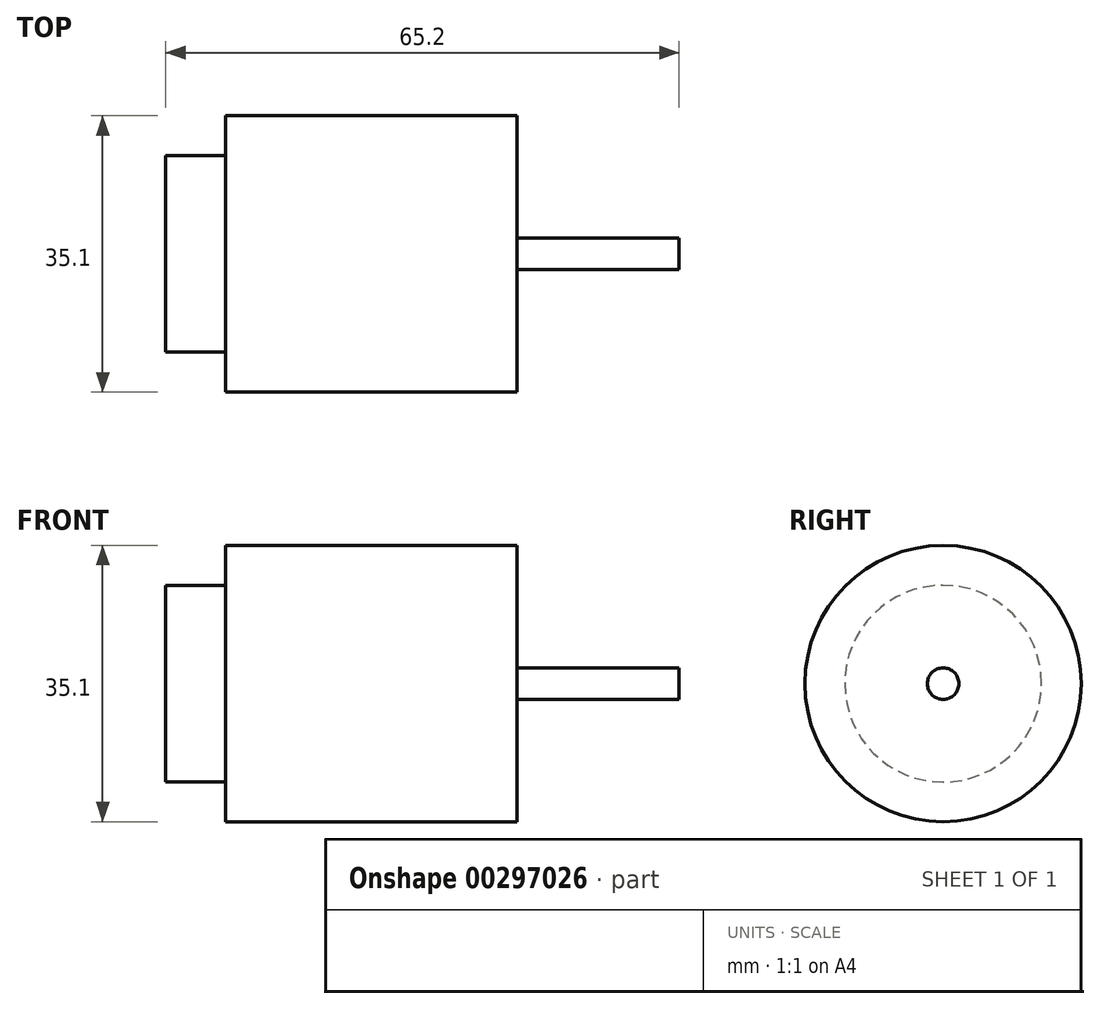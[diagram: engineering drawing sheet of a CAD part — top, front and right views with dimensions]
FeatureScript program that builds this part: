
annotation { "Feature Type Name" : "Feature", "Feature Type Description" : "" }
export const myFeature = defineFeature(function(context is Context, id is Id, definition is map)
    precondition{}
    {
        {
            var Q0;
            Q0=qCreatedBy(makeId("Front.planeOp"),FACE);
            var sketch = newSketch(context, id + "F0", { "sketchPlane" : qUnion([Q0])});
            skLineSegment(sketch, "E0.bottom", {"start": v(-37, 17.55) * mm, "end": v(0, 17.55) * mm});
            skLineSegment(sketch, "E0.top", {"start": v(-37, -17.55) * mm, "end": v(0, -17.55) * mm});
            skLineSegment(sketch, "E0.left", {"start": v(-37, 17.55) * mm, "end": v(-37, -17.55) * mm});
            skLineSegment(sketch, "E0.right", {"start": v(0, 17.55) * mm, "end": v(0, -17.55) * mm});
            skLineSegment(sketch, "E1.bottom", {"start": v(-44.6, -12.5) * mm, "end": v(-37, -12.5) * mm});
            skLineSegment(sketch, "E1.top", {"start": v(-44.6, 12.5) * mm, "end": v(-37, 12.5) * mm});
            skLineSegment(sketch, "E1.left", {"start": v(-44.6, 12.5) * mm, "end": v(-44.6, -12.5) * mm});
            skLineSegment(sketch, "E1.right", {"start": v(-37, 12.5) * mm, "end": v(-37, -12.5) * mm});
            skLineSegment(sketch, "E2", {"start": v(0, 0) * mm, "end": v(-44.6, 0) * mm});
            skLineSegment(sketch, "E3.bottom", {"start": v(0, -2) * mm, "end": v(20.6, -2) * mm});
            skLineSegment(sketch, "E3.top", {"start": v(0, 2) * mm, "end": v(20.6, 2) * mm});
            skLineSegment(sketch, "E3.left", {"start": v(0, 2) * mm, "end": v(0, -2) * mm});
            skLineSegment(sketch, "E3.right", {"start": v(20.6, 2) * mm, "end": v(20.6, -2) * mm});
            skLineSegment(sketch, "E4", {"start": v(0, 0) * mm, "end": v(20.6, 0) * mm});
            skSolve(sketch);
        }
        {
            var Q0;
            {var subQ0=sQuery(id+"F0.wireOp",EDGE,"E1.top");Q0=makeQuery(id+"F0.imprint","IMPRINT",FACE,{"disambiguationData":[TD([[makeQuery(id+"F0.imprint","IMPRINT",EDGE,{"derivedFrom":subQ0}),-1.0]])]});}
            var Q1;
            {var subQ1=sQuery(id+"F0.wireOp",EDGE,"E0.bottom");Q1=makeQuery(id+"F0.imprint","IMPRINT",FACE,{"disambiguationData":[TD([[makeQuery(id+"F0.imprint","IMPRINT",EDGE,{"derivedFrom":subQ1}),-1.0]])]});}
            var Q2;
            {var subQ0=sQuery(id+"F0.wireOp",EDGE,"E3.top");Q2=makeQuery(id+"F0.imprint","IMPRINT",FACE,{"disambiguationData":[TD([[makeQuery(id+"F0.imprint","IMPRINT",EDGE,{"derivedFrom":subQ0}),-1.0]])]});}
            var Q3;
            Q3=sQuery(id+"F0.wireOp",EDGE,"E2");
            revolve(context, id + "F1", {"entities" : qUnion([Q0, Q1, Q2]), "axis" : qUnion([Q3]), "revolveType" : RevolveType.FULL});
        }
    });
